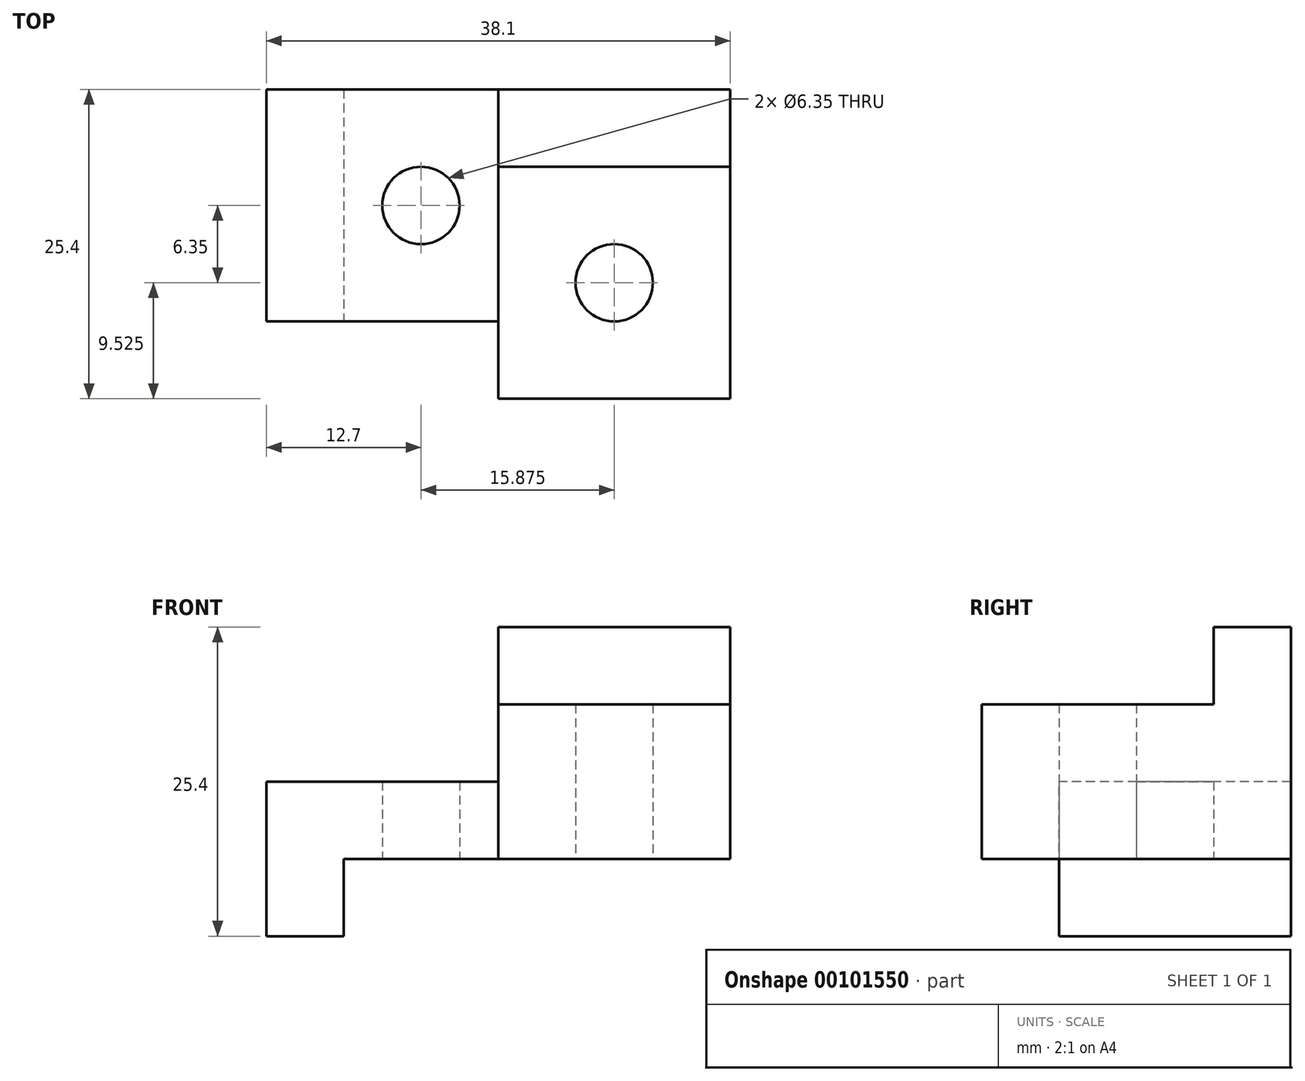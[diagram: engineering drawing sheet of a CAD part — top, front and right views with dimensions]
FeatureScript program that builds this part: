
annotation { "Feature Type Name" : "Feature", "Feature Type Description" : "" }
export const myFeature = defineFeature(function(context is Context, id is Id, definition is map)
    precondition{}
    {
        {
            var Q0;
            Q0=qCreatedBy(makeId("Top.planeOp"),FACE);
            var sketch = newSketch(context, id + "F0", { "sketchPlane" : qUnion([Q0])});
            skLineSegment(sketch, "E0", {"start": v(0, 0) * mm, "end": v(0, 19.05) * mm});
            skLineSegment(sketch, "E1", {"start": v(0, 19.05) * mm, "end": v(38.1, 19.05) * mm});
            skLineSegment(sketch, "E2", {"start": v(38.1, 19.05) * mm, "end": v(38.1, -6.35) * mm});
            skLineSegment(sketch, "E3", {"start": v(38.1, -6.35) * mm, "end": v(19.05, -6.35) * mm});
            skLineSegment(sketch, "E4", {"start": v(19.05, -6.35) * mm, "end": v(19.05, 0) * mm});
            skLineSegment(sketch, "E5", {"start": v(19.05, 0) * mm, "end": v(0, 0) * mm});
            skLineSegment(sketch, "E6", {"start": v(19.05, 19.05) * mm, "end": v(19.05, 12.7) * mm});
            skLineSegment(sketch, "E7", {"start": v(19.05, 12.7) * mm, "end": v(38.1, 12.7) * mm});
            skLineSegment(sketch, "E8", {"start": v(6.35, 19.05) * mm, "end": v(6.35, 0) * mm});
            skLineSegment(sketch, "E9", {"start": v(19.05, 12.7) * mm, "end": v(19.05, 0) * mm});
            skCircle(sketch, "E10", {"center": v(28.58, 3.17) * mm, "radius": 3.18 * mm});
            skPoint(sketch, "E11.centerSnap0", {"position": v(19.05, 6.35) * mm});
            skCircle(sketch, "E12", {"center": v(12.7, 9.53) * mm, "radius": 3.18 * mm});
            skSolve(sketch);
        }
        {
            var Q0;
            {var subQ1=sQuery(id+"F0.wireOp",EDGE,"E3");Q0=makeQuery(id+"F0.imprint","IMPRINT",FACE,{"disambiguationData":[TD([[makeQuery(id+"F0.imprint","IMPRINT",EDGE,{"derivedFrom":subQ1}),-1.0]])]});}
            extrude(context, id + "F1", {"entities" : qUnion([Q0]), "depth" : 12.7 * mm});
        }
        {
            var Q0;
            {var subQ3=sQuery(id+"F0.wireOp",EDGE,"E6");Q0=makeQuery(id+"F0.imprint","IMPRINT",FACE,{"disambiguationData":[TD([[makeQuery(id+"F0.imprint","IMPRINT",EDGE,{"derivedFrom":subQ3}),1.0]])]});}
            extrude(context, id + "F2", {"entities" : qUnion([Q0]), "operationType" : NewBodyOperationType.ADD, "depth" : 19.05 * mm});
        }
        {
            var Q0;
            {var subQ1=sQuery(id+"F0.wireOp",EDGE,"E6");Q0=makeQuery(id+"F0.imprint","IMPRINT",FACE,{"disambiguationData":[TD([[makeQuery(id+"F0.imprint","IMPRINT",EDGE,{"derivedFrom":subQ1}),-1.0]])]});}
            extrude(context, id + "F3", {"entities" : qUnion([Q0]), "operationType" : NewBodyOperationType.ADD, "depth" : 6.35 * mm});
        }
        {
            var Q0;
            {var subQ0=sQuery(id+"F0.wireOp",EDGE,"E0");Q0=makeQuery(id+"F0.imprint","IMPRINT",FACE,{"disambiguationData":[TD([[makeQuery(id+"F0.imprint","IMPRINT",EDGE,{"derivedFrom":subQ0}),-1.0]])]});}
            extrude(context, id + "F4", {"entities" : qUnion([Q0]), "operationType" : NewBodyOperationType.ADD, "endBound" : BoundingType.SYMMETRIC, "oppositeDirection" : true, "depth" : 12.7 * mm});
        }
    });
